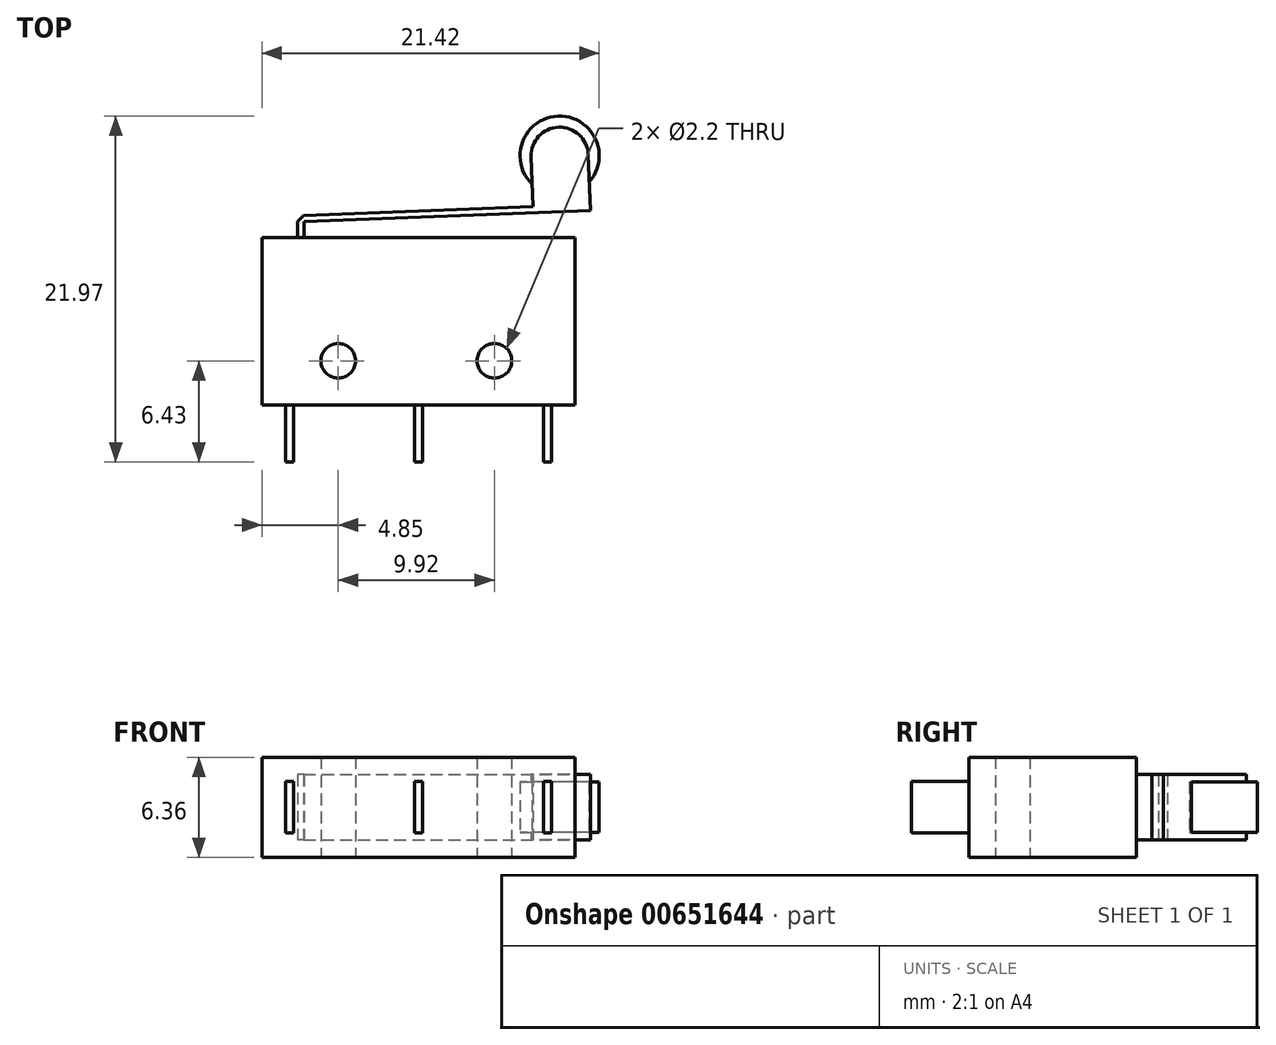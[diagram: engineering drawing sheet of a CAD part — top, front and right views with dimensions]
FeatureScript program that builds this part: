
annotation { "Feature Type Name" : "Feature", "Feature Type Description" : "" }
export const myFeature = defineFeature(function(context is Context, id is Id, definition is map)
    precondition{}
    {
        {
            var Q0;
            Q0=qCreatedBy(makeId("Top.planeOp"),FACE);
            var sketch = newSketch(context, id + "F0", { "sketchPlane" : qUnion([Q0])});
            skLineSegment(sketch, "E0.bottom", {"start": v(9.95, -5.32) * mm, "end": v(8.45, -5.32) * mm});
            skLineSegment(sketch, "E0.top", {"start": v(9.95, 5.32) * mm, "end": v(-7.28, 5.32) * mm});
            skLineSegment(sketch, "E0.left", {"start": v(9.95, -5.32) * mm, "end": v(9.95, 5.32) * mm});
            skLineSegment(sketch, "E0.right", {"start": v(-9.95, -5.32) * mm, "end": v(-9.95, 5.32) * mm});
            skPoint(sketch, "E0.middle", {"position": v(0, 0) * mm});
            skLineSegment(sketch, "E1.bottom", {"start": v(-8.45, -5.32) * mm, "end": v(-7.95, -5.32) * mm});
            skLineSegment(sketch, "E1.top", {"start": v(-8.45, -8.95) * mm, "end": v(-7.95, -8.95) * mm});
            skLineSegment(sketch, "E1.left", {"start": v(-8.45, -5.32) * mm, "end": v(-8.45, -8.95) * mm});
            skLineSegment(sketch, "E1.right", {"start": v(-7.95, -5.32) * mm, "end": v(-7.95, -8.95) * mm});
            skLineSegment(sketch, "E2.bottom", {"start": v(-0.25, -5.32) * mm, "end": v(0.25, -5.32) * mm});
            skLineSegment(sketch, "E2.top", {"start": v(-0.25, -8.95) * mm, "end": v(0.25, -8.95) * mm});
            skLineSegment(sketch, "E2.left", {"start": v(-0.25, -5.32) * mm, "end": v(-0.25, -8.95) * mm});
            skLineSegment(sketch, "E2.right", {"start": v(0.25, -5.32) * mm, "end": v(0.25, -8.95) * mm});
            skLineSegment(sketch, "E3.bottom", {"start": v(7.95, -5.32) * mm, "end": v(8.45, -5.32) * mm});
            skLineSegment(sketch, "E3.top", {"start": v(7.95, -8.95) * mm, "end": v(8.45, -8.95) * mm});
            skLineSegment(sketch, "E3.left", {"start": v(7.95, -5.32) * mm, "end": v(7.95, -8.95) * mm});
            skLineSegment(sketch, "E3.right", {"start": v(8.45, -5.32) * mm, "end": v(8.45, -8.95) * mm});
            skLineSegment(sketch, "E4", {"start": v(8.45, -5.32) * mm, "end": v(7.95, -5.32) * mm});
            skLineSegment(sketch, "E5", {"start": v(-8.45, -5.32) * mm, "end": v(-9.95, -5.32) * mm});
            skLineSegment(sketch, "E6", {"start": v(-7.95, -5.32) * mm, "end": v(-8.45, -5.32) * mm});
            skLineSegment(sketch, "E7", {"start": v(-0.25, -5.32) * mm, "end": v(-7.95, -5.32) * mm});
            skLineSegment(sketch, "E8", {"start": v(0.25, -5.32) * mm, "end": v(-0.25, -5.32) * mm});
            skLineSegment(sketch, "E9", {"start": v(7.95, -5.32) * mm, "end": v(0.25, -5.32) * mm});
            skLineSegment(sketch, "E10", {"start": v(-7.28, 6.32) * mm, "end": v(10.9, 7.03) * mm});
            skLineSegment(sketch, "E11", {"start": v(10.9, 7.03) * mm, "end": v(10.77, 10.58) * mm});
            skLineSegment(sketch, "E12", {"start": v(7.27, 7.3) * mm, "end": v(7.15, 10.44) * mm});
            skArc(sketch, "E13", {"start": v(10.77, 10.58) * mm, "mid": v(8.89, 12.32) * mm, "end": v(7.15, 10.44) * mm});
            skCircle(sketch, "E14", {"center": v(8.96, 10.5) * mm, "radius": 2.52 * mm});
            skLineSegment(sketch, "E15", {"start": v(-7.28, 6.32) * mm, "end": v(-7.28, 5.32) * mm});
            skLineSegment(sketch, "E16", {"start": v(-7.68, 5.32) * mm, "end": v(-7.68, 6.32) * mm});
            skLineSegment(sketch, "E17", {"start": v(-7.68, 5.32) * mm, "end": v(-9.95, 5.32) * mm});
            skLineSegment(sketch, "E18", {"start": v(-7.28, 5.32) * mm, "end": v(-7.68, 5.32) * mm});
            skLineSegment(sketch, "E19", {"start": v(-7.28, 6.32) * mm, "end": v(-7.3, 6.72) * mm, "construction": true});
            skLineSegment(sketch, "E20", {"start": v(-7.3, 6.72) * mm, "end": v(7.27, 7.3) * mm});
            skLineSegment(sketch, "E21", {"start": v(-7.3, 6.72) * mm, "end": v(-7.68, 6.32) * mm});
            skLineSegment(sketch, "E22", {"start": v(0, 0) * mm, "end": v(0, 5.32) * mm, "construction": true});
            skLineSegment(sketch, "E23", {"start": v(0, 5.32) * mm, "end": v(0, 0) * mm});
            skLineSegment(sketch, "E24", {"start": v(0, 0) * mm, "end": v(0, -5.32) * mm, "construction": true});
            skCircle(sketch, "E25", {"center": v(-5.1, -2.52) * mm, "radius": 1.1 * mm});
            skCircle(sketch, "E26", {"center": v(4.82, -2.52) * mm, "radius": 1.1 * mm});
            skSolve(sketch);
        }
        {
            var Q0;
            Q0=makeQuery(id+"F0.imprint","IMPRINT",FACE,{"disambiguationData":[TD([[makeQuery(id+"F0.imprint","IMPRINT",EDGE,{"derivedFrom":sQuery(id+"F0.wireOp",EDGE,"E0.bottom")}),-1.0]])]});
            extrude(context, id + "F1", {"entities" : qUnion([Q0]), "depth" : (6.35 / 2) * mm, "offsetDistance" : 25 * mm, "hasSecondDirection" : true, "secondDirectionOppositeDirection" : true, "secondDirectionDepth" : (6.35 / 2) * mm});
        }
        {
            var Q0;
            {var subQ6=sQuery(id+"F0.wireOp",EDGE,"E10");Q0=makeQuery(id+"F0.imprint","IMPRINT",FACE,{"disambiguationData":[TD([[makeQuery(id+"F0.imprint","IMPRINT",EDGE,{"derivedFrom":subQ6}),1.0]])]});}
            var Q1;
            {var subQ0=sQuery(id+"F0.wireOp",EDGE,"E13");Q1=makeQuery(id+"F0.imprint","IMPRINT",FACE,{"disambiguationData":[TD([[makeQuery(id+"F0.imprint","IMPRINT",EDGE,{"derivedFrom":subQ0}),1.0]])]});}
            extrude(context, id + "F2", {"entities" : qUnion([Q0, Q1]), "operationType" : NewBodyOperationType.ADD, "depth" : (4.15 / 2) * mm, "offsetDistance" : 25 * mm, "hasSecondDirection" : true, "secondDirectionOppositeDirection" : true, "secondDirectionDepth" : (4.15 / 2) * mm});
        }
        {
            var Q0;
            Q0=makeQuery(id+"F0.imprint","IMPRINT",FACE,{"disambiguationData":[TD([[makeQuery(id+"F0.imprint","IMPRINT",EDGE,{"derivedFrom":sQuery(id+"F0.wireOp",EDGE,"E1.top")}),1.0]])]});
            var Q1;
            Q1=makeQuery(id+"F0.imprint","IMPRINT",FACE,{"disambiguationData":[TD([[makeQuery(id+"F0.imprint","IMPRINT",EDGE,{"derivedFrom":sQuery(id+"F0.wireOp",EDGE,"E3.top")}),1.0]])]});
            var Q2;
            Q2=makeQuery(id+"F0.imprint","IMPRINT",FACE,{"disambiguationData":[TD([[makeQuery(id+"F0.imprint","IMPRINT",EDGE,{"derivedFrom":sQuery(id+"F0.wireOp",EDGE,"E2.top")}),1.0]])]});
            extrude(context, id + "F3", {"entities" : qUnion([Q0, Q1, Q2]), "operationType" : NewBodyOperationType.ADD, "depth" : (3.27 / 2) * mm, "offsetDistance" : 25 * mm, "hasSecondDirection" : true, "secondDirectionOppositeDirection" : true, "secondDirectionDepth" : (3.27 / 2) * mm});
        }
        {
            var Q0;
            {var subQ0=sQuery(id+"F0.wireOp",EDGE,"E13");Q0=makeQuery(id+"F0.imprint","IMPRINT",FACE,{"disambiguationData":[TD([[makeQuery(id+"F0.imprint","IMPRINT",EDGE,{"derivedFrom":subQ0}),-1.0]])]});}
            extrude(context, id + "F4", {"entities" : qUnion([Q0]), "operationType" : NewBodyOperationType.ADD, "depth" : (3.2 / 2) * mm, "offsetDistance" : 25 * mm, "hasSecondDirection" : true, "secondDirectionOppositeDirection" : true, "secondDirectionDepth" : (3.2 / 2) * mm});
        }
    });
